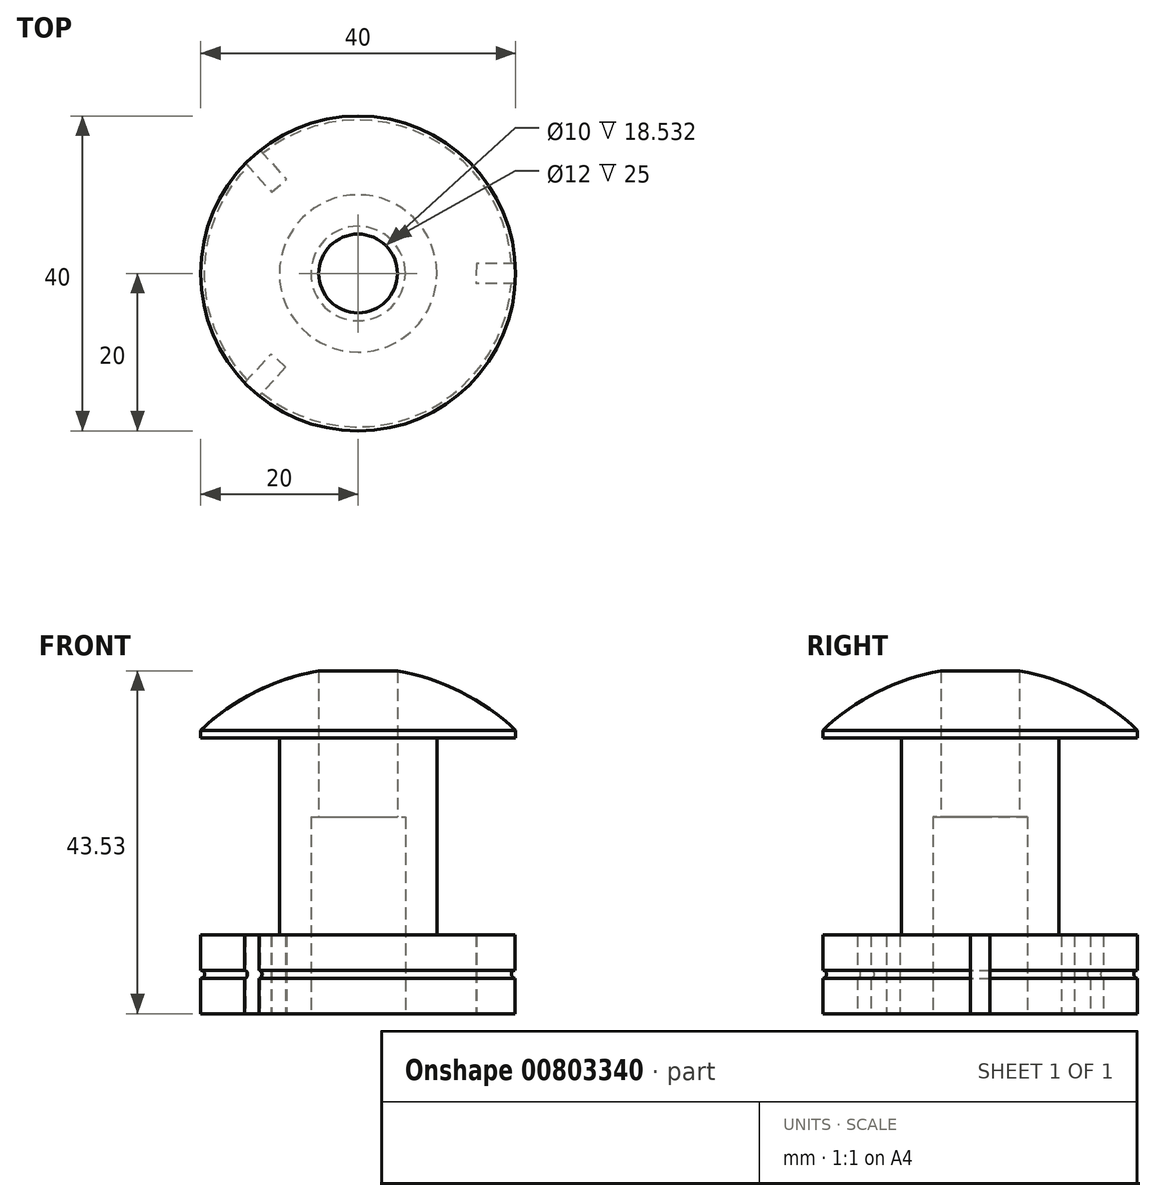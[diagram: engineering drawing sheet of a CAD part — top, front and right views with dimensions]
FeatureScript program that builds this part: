
annotation { "Feature Type Name" : "Feature", "Feature Type Description" : "" }
export const myFeature = defineFeature(function(context is Context, id is Id, definition is map)
    precondition{}
    {
        {
            var Q0;
            Q0=qCreatedBy(makeId("Front.planeOp"),FACE);
            var sketch = newSketch(context, id + "F0", { "sketchPlane" : qUnion([Q0])});
            skLineSegment(sketch, "E0.bottom", {"start": v(0, 0) * mm, "end": v(40, 0) * mm});
            skLineSegment(sketch, "E0.top", {"start": v(0, 10) * mm, "end": v(10, 10) * mm});
            skLineSegment(sketch, "E0.left", {"start": v(0, 0) * mm, "end": v(0, 10) * mm});
            skLineSegment(sketch, "E0.right", {"start": v(40, 0) * mm, "end": v(40, 10) * mm});
            skLineSegment(sketch, "E1.left", {"start": v(10, 10) * mm, "end": v(10, 35) * mm});
            skLineSegment(sketch, "E1.right", {"start": v(30, 10) * mm, "end": v(30, 35) * mm});
            skLineSegment(sketch, "E2.top", {"start": v(0, 35) * mm, "end": v(10, 35) * mm});
            skLineSegment(sketch, "E2.left", {"start": v(0, 36) * mm, "end": v(0, 35) * mm});
            skLineSegment(sketch, "E2.right", {"start": v(40, 36) * mm, "end": v(40, 35) * mm});
            skLineSegment(sketch, "E3.trimOffspring", {"start": v(30, 35) * mm, "end": v(40, 35) * mm});
            skLineSegment(sketch, "E4.trimOffspring", {"start": v(30, 10) * mm, "end": v(40, 10) * mm});
            skArc(sketch, "E5", {"start": v(40, 36) * mm, "mid": v(20, 43.96) * mm, "end": v(0, 36) * mm});
            skLineSegment(sketch, "E6", {"start": v(20, 0) * mm, "end": v(20, 43.96) * mm});
            skCircle(sketch, "E7", {"center": v(0, 5) * mm, "radius": 0.5 * mm});
            skCircle(sketch, "E8", {"center": v(40, 5) * mm, "radius": 0.5 * mm});
            skSolve(sketch);
        }
        {
            var Q0;
            Q0=makeQuery(id+"F0.imprint","IMPRINT",FACE,{"disambiguationData":[TD([[makeQuery(id+"F0.imprint","IMPRINT",EDGE,{"derivedFrom":sQuery(id+"F0.wireOp",EDGE,"E0.top")}),-1.0]])]});
            var Q1;
            Q1=sQuery(id+"F0.wireOp",EDGE,"E6");
            revolve(context, id + "F1", {"surfaceOperationType" : NewSurfaceOperationType.NEW, "entities" : qUnion([Q0]), "axis" : qUnion([Q1]), "revolveType" : RevolveType.FULL});
        }
        {
            var Q0;
            Q0=makeQuery(id+"F1.opRevolve","SWEPT_FACE",FACE,{"disambiguationData":[OSD([sQuery(id+"F0.wireOp",EDGE,"E0.bottom")])]});
            var sketch = newSketch(context, id + "F2", { "sketchPlane" : qUnion([Q0])});
            skCircle(sketch, "E9", {"center": v(20, 0) * mm, "radius": 5 * mm});
            skSolve(sketch);
        }
        {
            var Q0;
            Q0 = qSketchRegion(id + "F2", true);
            extrude(context, id + "F3", {"entities" : qUnion([Q0]), "operationType" : NewBodyOperationType.REMOVE, "oppositeDirection" : true, "depth" : 43.96 * mm, "offsetDistance" : 25 * mm});
        }
        {
            var Q0;
            Q0=makeQuery(id+"F1.opRevolve","SWEPT_FACE",FACE,{"disambiguationData":[OSD([sQuery(id+"F0.wireOp",EDGE,"E0.bottom")])]});
            var sketch = newSketch(context, id + "F4", { "sketchPlane" : qUnion([Q0])});
            skCircle(sketch, "E10", {"center": v(20, 0) * mm, "radius": 6 * mm});
            skLineSegment(sketch, "E11.left", {"start": v(10.79, 11.9) * mm, "end": v(6.73, 16.33) * mm});
            skPoint(sketch, "E11.middle", {"position": v(5.42, 16.92) * mm});
            skLineSegment(sketch, "E12.bottom", {"start": v(41.04, -1.25) * mm, "end": v(35.04, -1.25) * mm});
            skLineSegment(sketch, "E12.top", {"start": v(40.97, 1.25) * mm, "end": v(34.97, 1.25) * mm});
            skLineSegment(sketch, "E12.left", {"start": v(41.04, -1.25) * mm, "end": v(40.97, 1.25) * mm});
            skLineSegment(sketch, "E12.right", {"start": v(35.04, -1.25) * mm, "end": v(34.97, 1.25) * mm});
            skLineSegment(sketch, "E13", {"start": v(6.73, 16.33) * mm, "end": v(4.9, 14.64) * mm});
            skLineSegment(sketch, "E14", {"start": v(4.9, 14.64) * mm, "end": v(8.94, 10.21) * mm});
            skLineSegment(sketch, "E15", {"start": v(10.79, 11.9) * mm, "end": v(8.94, 10.21) * mm});
            skLineSegment(sketch, "E16", {"start": v(5.02, -14.77) * mm, "end": v(9.03, -10.3) * mm});
            skLineSegment(sketch, "E17", {"start": v(9.03, -10.3) * mm, "end": v(10.9, -11.98) * mm});
            skLineSegment(sketch, "E18", {"start": v(5.02, -14.77) * mm, "end": v(6.87, -16.44) * mm});
            skLineSegment(sketch, "E19", {"start": v(6.87, -16.44) * mm, "end": v(10.9, -11.98) * mm});
            skSolve(sketch);
        }
        {
            var Q0;
            Q0 = qSketchRegion(id + "F4", true);
            extrude(context, id + "F5", {"entities" : qUnion([Q0]), "operationType" : NewBodyOperationType.REMOVE, "oppositeDirection" : true, "depth" : 25 * mm, "offsetDistance" : 25 * mm});
        }
    });
